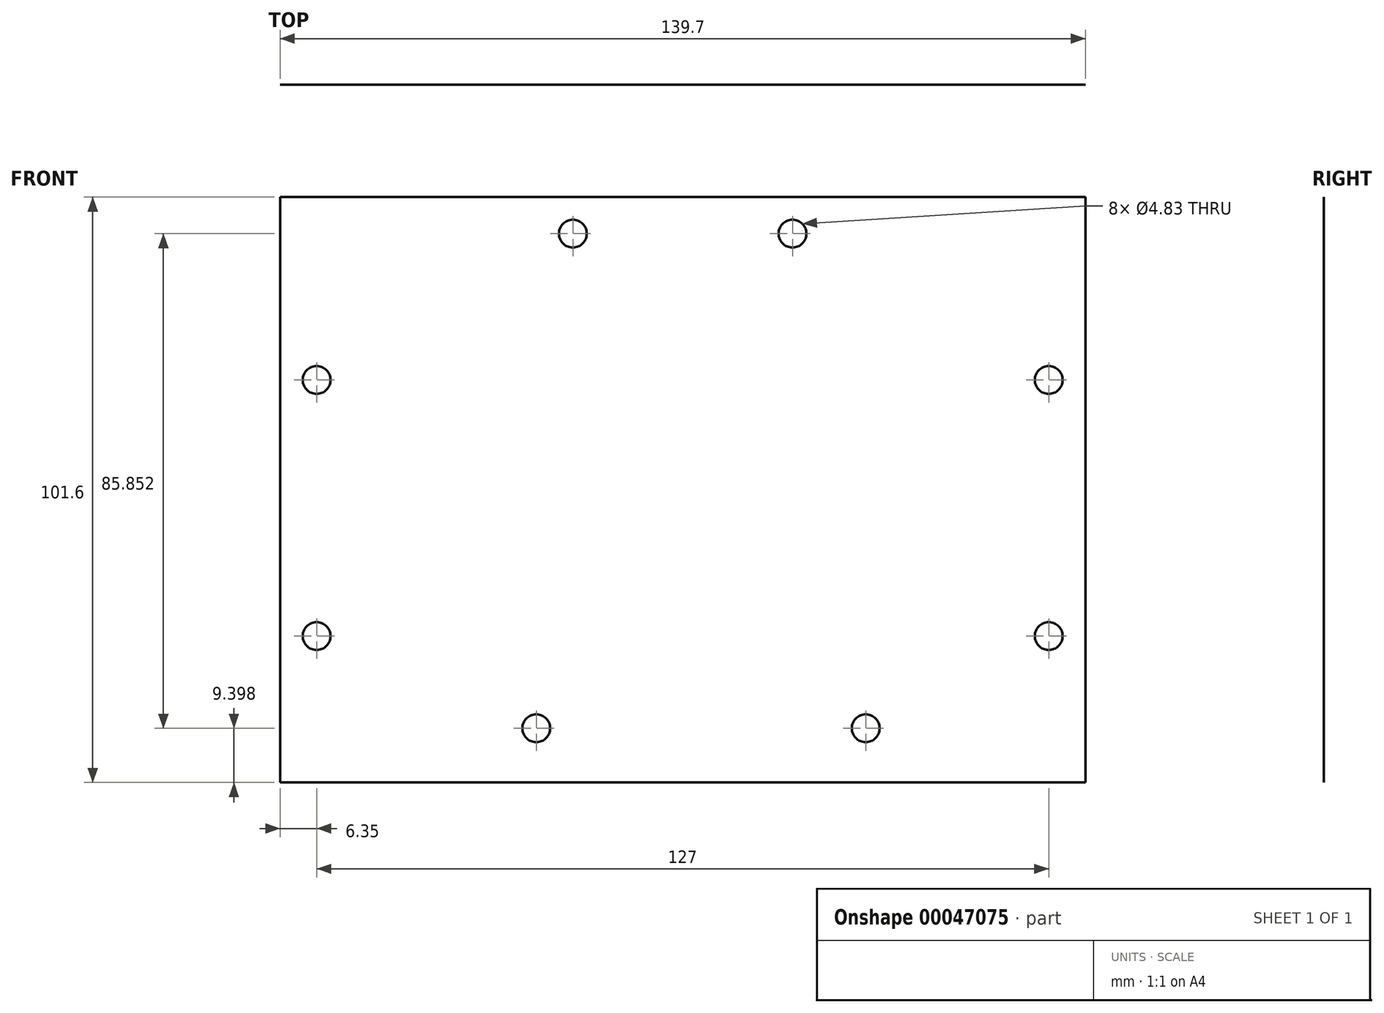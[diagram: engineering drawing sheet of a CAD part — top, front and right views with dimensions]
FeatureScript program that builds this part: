
annotation { "Feature Type Name" : "Feature", "Feature Type Description" : "" }
export const myFeature = defineFeature(function(context is Context, id is Id, definition is map)
    precondition{}
    {
        {
            var Q0;
            Q0=qCreatedBy(makeId("Front.planeOp"),FACE);
            var sketch = newSketch(context, id + "F0", { "sketchPlane" : qUnion([Q0])});
            skLineSegment(sketch, "E0.rect.bottom", {"start": v(69.85, 50.8) * mm, "end": v(-69.85, 50.8) * mm});
            skLineSegment(sketch, "E0.rect.top", {"start": v(69.85, -50.8) * mm, "end": v(-69.85, -50.8) * mm});
            skLineSegment(sketch, "E0.rect.left", {"start": v(69.85, 50.8) * mm, "end": v(69.85, -50.8) * mm});
            skLineSegment(sketch, "E0.rect.right", {"start": v(-69.85, 50.8) * mm, "end": v(-69.85, -50.8) * mm});
            skPoint(sketch, "E0.rect.middle", {"position": v(0, 0) * mm});
            skSolve(sketch);
        }
        {
            var Q0;
            Q0 = qSketchRegion(id + "F0", true);
            extrude(context, id + "F1", {"entities" : qUnion([Q0]), "endBound" : BoundingType.SYMMETRIC, "depth" : 1 / 203.2 * mm});
        }
        {
            var Q0;
            Q0=makeQuery(id+"F1.opExtrude","CAP_FACE",FACE,{"disambiguationData":[OSD([sQuery(id+"F0.wireOp",EDGE,"E0.rect.bottom"),sQuery(id+"F0.wireOp",EDGE,"E0.rect.top"),sQuery(id+"F0.wireOp",EDGE,"E0.rect.left"),sQuery(id+"F0.wireOp",EDGE,"E0.rect.right")])],"isStart":false});
            var sketch = newSketch(context, id + "F2", { "sketchPlane" : qUnion([Q0])});
            skCircle(sketch, "E1", {"center": v(-63.5, 19.05) * mm, "radius": 2.41 * mm});
            skCircle(sketch, "E2", {"center": v(-63.5, -25.4) * mm, "radius": 2.41 * mm});
            skCircle(sketch, "E3.MirrorC", {"center": v(63.5, -25.4) * mm, "radius": 2.41 * mm});
            skCircle(sketch, "E4.MirrorC", {"center": v(63.5, 19.05) * mm, "radius": 2.41 * mm});
            skCircle(sketch, "E5", {"center": v(-19.05, 44.45) * mm, "radius": 2.41 * mm});
            skCircle(sketch, "E6", {"center": v(19.05, 44.45) * mm, "radius": 2.41 * mm});
            skCircle(sketch, "E7", {"center": v(-25.4, -41.4) * mm, "radius": 2.41 * mm});
            skCircle(sketch, "E8", {"center": v(31.75, -41.4) * mm, "radius": 2.41 * mm});
            skSolve(sketch);
        }
        {
            var Q0;
            Q0 = qSketchRegion(id + "F2", true);
            var Q1;
            Q1=makeQuery(id+"F1.opExtrude","CAP_FACE",FACE,{"disambiguationData":[OSD([sQuery(id+"F0.wireOp",EDGE,"E0.rect.bottom"),sQuery(id+"F0.wireOp",EDGE,"E0.rect.top"),sQuery(id+"F0.wireOp",EDGE,"E0.rect.left"),sQuery(id+"F0.wireOp",EDGE,"E0.rect.right")])],"isStart":true});
            extrude(context, id + "F3", {"entities" : qUnion([Q0]), "operationType" : NewBodyOperationType.REMOVE, "endBound" : BoundingType.UP_TO_SURFACE, "oppositeDirection" : true, "endBoundEntityFace" : qUnion([Q1]), "depth" : 25.4 * mm});
        }
    });
